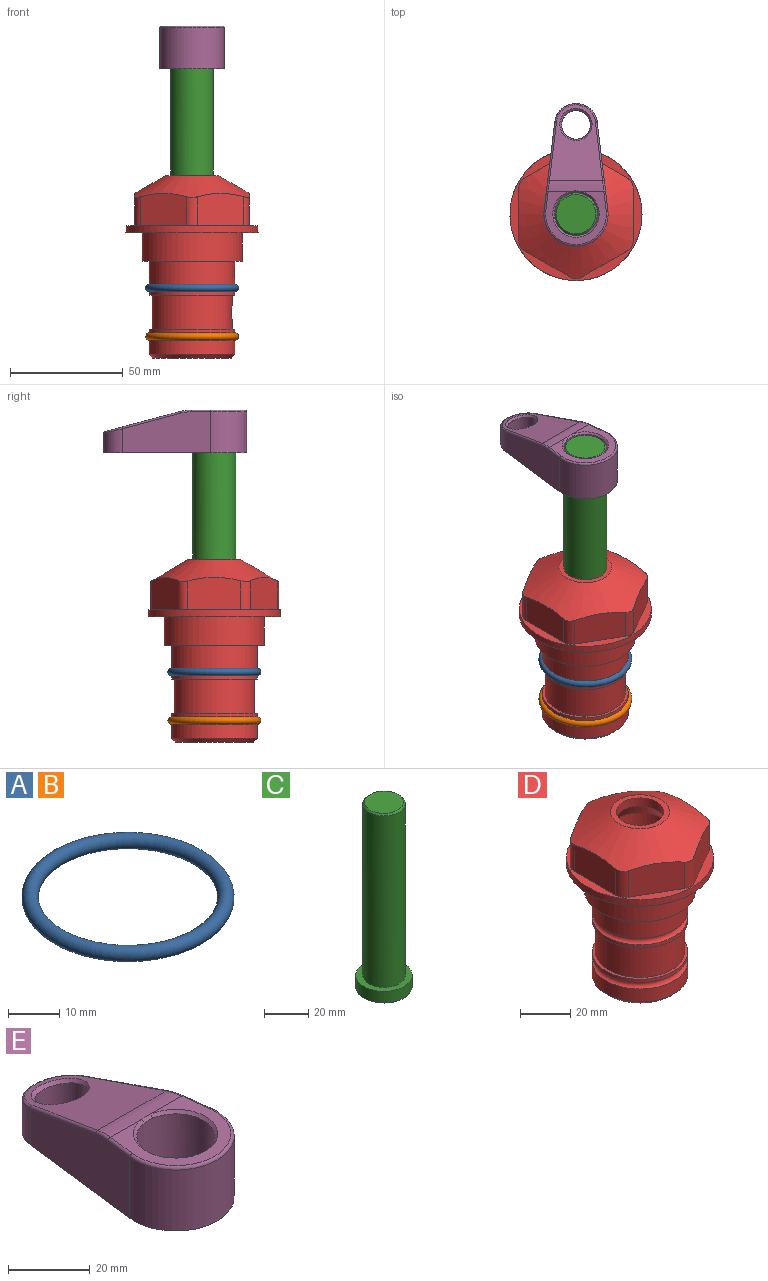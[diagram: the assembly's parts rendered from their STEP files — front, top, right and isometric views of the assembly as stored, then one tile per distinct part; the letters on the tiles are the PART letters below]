
ASSEMBLY  parts=5 mates=4
PART A: 1 faces, bbox 44.7x44.7x3.2 mm
  f0: torus R=19.05mm, axis (0,0,1), area 1193.9mm2
PART B: same geometry as A
PART C: 6 faces, bbox 25.4x25.4x101.6 mm
  f0: plane 17.46x17.46mm, normal (0,0,1), area 239.5mm2, adj f5
  f1: plane 25.4x25.4mm, normal (0,0,-1), area 506.7mm2, adj f2
  f2: cylinder r=12.7mm len=25.4mm, axis (0,0,1), area 506.7mm2, adj f1,f3
  f3: plane 25.4x25.4mm, normal (0,0,1), area 221.7mm2, adj f2,f4
  f4: cylinder r=9.53mm len=94.46mm, axis (0,0,1), area 5653mm2, adj f3,f5
  f5: cone r=8.73mm half-angle=45deg, axis (0,0,-1), area 64.4mm2, adj f0,f4
PART D: 36 faces, bbox 58.7x58.7x81 mm
  f0: cylinder r=17.78mm len=35.56mm, axis (0,0,1), area 1670.8mm2, adj f23,f24,f31
  f1: cylinder r=19.05mm len=38.1mm, axis (0,0,1), area 1191.9mm2, adj f26,f27,f30
  f2: plane 58.66x58.66mm, normal (0,0,-1), area 1150.6mm2, adj f3,f28
  f3: cylinder r=29.33mm len=58.66mm, axis (0,0,-1), area 585.1mm2, adj f2,f4
  f4: plane 58.66x58.66mm, normal (0,0,1), area 475.9mm2, adj f3,f5,f6,f7,f8,f9,f10,f11
  f5: plane 20.32x14.34mm, normal (-0.5,0.87,0), area 324.4mm2, adj f4,f15,f16,f17
  f6: plane 20.32x14.34mm, normal (0.5,0.87,0), area 324.4mm2, adj f4,f14,f15,f17
  f7: plane 23.48x14.34mm, normal (1,0,0), area 324.4mm2, adj f4,f13,f14,f17
  f8: plane 20.32x14.34mm, normal (0.5,-0.87,0), area 324.4mm2, adj f4,f12,f13,f17
  f9: plane 20.32x14.34mm, normal (-0.5,-0.87,0), area 324.4mm2, adj f4,f11,f12,f17
  f10: plane 23.48x14.34mm, normal (-1,0,0), area 324.4mm2, adj f4,f11,f16,f17
  f11: cylinder r=5.08mm len=12.85mm, axis (0,0,-1), area 67.2mm2, adj f4,f9,f10,f17
  f12: cylinder r=5.08mm len=12.85mm, axis (0,0,-1), area 67.2mm2, adj f4,f8,f9,f17
  f13: cylinder r=5.08mm len=12.85mm, axis (0,0,-1), area 67.2mm2, adj f4,f7,f8,f17
  f14: cylinder r=5.08mm len=12.85mm, axis (0,0,-1), area 67.2mm2, adj f4,f6,f7,f17
  f15: cylinder r=5.08mm len=12.85mm, axis (0,0,-1), area 67.2mm2, adj f4,f5,f6,f17
  f16: cylinder r=5.08mm len=12.85mm, axis (0,0,-1), area 67.2mm2, adj f4,f5,f10,f17
  f17: cone r=11.73mm half-angle=60deg, axis (0,0,-1), area 2071.8mm2, adj f5,f6,f7,f8,f9,f10,f11,f12
  f18: plane 23.46x23.46mm, normal (0,0,1), area 147.4mm2, adj f17,f35
  f19: plane 34.93x34.93mm, normal (0,0,-1), area 958mm2, adj f29
  f20: cylinder r=19.05mm len=38.1mm, axis (0,0,1), area 760.1mm2, adj f21,f29
  f21: torus R=19.05mm, axis (0,0,1), area 565.3mm2, adj f20,f22
  f22: cylinder r=19.05mm len=38.1mm, axis (0,0,1), area 190mm2, adj f21,f23
  f23: plane 38.1x38.1mm, normal (0,0,1), area 146.9mm2, adj f0,f22
  f24: plane 38.1x38.1mm, normal (0,0,-1), area 146.9mm2, adj f0,f25
  f25: cylinder r=19.05mm len=38.1mm, axis (0,0,1), area 190mm2, adj f24,f26
  f26: torus R=19.05mm, axis (0,0,1), area 565.3mm2, adj f1,f25
  f27: plane 44.45x44.45mm, normal (0,0,-1), area 411.7mm2, adj f1,f28
  f28: cylinder r=22.23mm len=44.45mm, axis (0,0,1), area 1773.5mm2, adj f2,f27
  f29: cone r=19.05mm half-angle=45deg, axis (0,0,1), area 257.5mm2, adj f19,f20
  f30: cylinder r=3.17mm len=6.75mm, axis (-1,0,0), area 128mm2, adj f1,f33
  f31: cylinder r=3.17mm len=6.35mm, axis (-1,0,0), area 102.5mm2, adj f0,f33
  f32: plane 25.4x25.4mm, normal (0,0,1), area 506.7mm2, adj f33
  f33: cylinder r=12.7mm len=66.42mm, axis (0,0,-1), area 5236.2mm2, adj f30,f31,f32,f34
  f34: cone r=9.53mm half-angle=30deg, axis (0,0,-1), area 443.4mm2, adj f33,f35
  f35: cylinder r=9.53mm len=19.05mm, axis (0,0,-1), area 240.9mm2, adj f18,f34
PART E: 31 faces, bbox 31.7x65.5x19.8 mm
  f0: plane 39.12x18.26mm, normal (0.99,0.12,0), area 612.2mm2, adj f1,f4,f7,f11,f13,f15
  f1: cylinder r=9.53mm len=18.91mm, axis (0,0,-1), area 296.1mm2, adj f0,f2,f7,f17
  f2: plane 39.12x18.26mm, normal (-0.99,0.12,0), area 612.2mm2, adj f1,f4,f7,f12,f14,f16
  f3: cylinder r=6.35mm len=12.7mm, axis (0,0,-1), area 362.4mm2, adj f7,f18
  f4: cylinder r=14.29mm len=28.58mm, axis (0,0,-1), area 882.2mm2, adj f0,f2,f7,f10
  f5: cylinder r=9.53mm len=19.05mm, axis (0,0,-1), area 1092.6mm2, adj f7,f19,f20
  f6: plane 26.99x23.69mm, normal (0,0,1), area 216.2mm2, adj f9,f10,f11,f12,f19
  f7: plane 63.5x28.58mm, normal (0,0,-1), area 661.8mm2, adj f0,f1,f2,f3,f4,f5,f22,f23
  f8: plane 33.52x23.6mm, normal (0,0.26,0.97), area 486mm2, adj f9,f15,f16,f17,f18
  f9: cylinder r=19.05mm len=24.72mm, axis (1,0,0), area 120.4mm2, adj f6,f8,f13,f14,f20
  f10: torus R=13.49mm, axis (0,0,1), area 59mm2, adj f4,f6,f11,f12
  f11: cylinder r=0.79mm len=8.67mm, axis (0.12,-0.99,0), area 10.8mm2, adj f0,f6,f10,f13
  f12: cylinder r=0.79mm len=8.67mm, axis (0.12,0.99,0), area 10.8mm2, adj f2,f6,f10,f14
  f13: bspline ~4.95x1.42mm, area 6.1mm2, adj f0,f9,f11,f15
  f14: bspline ~4.95x1.42mm, area 6.1mm2, adj f2,f9,f12,f16
  f15: cylinder r=0.79mm len=25.95mm, axis (0.12,-0.96,0.26), area 32.9mm2, adj f0,f8,f13,f17
  f16: cylinder r=0.79mm len=25.95mm, axis (0.12,0.96,-0.26), area 32.9mm2, adj f2,f8,f14,f17
  f17: bspline ~18.91x8.38mm, area 30mm2, adj f1,f8,f15,f16
  f18: bspline ~14.29x14.29mm, area 48.3mm2, adj f3,f8
  f19: cone r=9.53mm half-angle=45deg, axis (0,0,1), area 66.5mm2, adj f5,f6,f20
  f20: bspline ~3.22x0.96mm, area 3.5mm2, adj f5,f9,f19
  f21: plane 2.75x2.72mm, normal (0,0,-1), area 2.9mm2, adj f23,f25,f28
  f22: plane 23.05x15.88mm, normal (-0.99,-0.12,0), area 323.6mm2, adj f7,f25,f26,f27,f28,f29
  f23: plane 23.05x15.88mm, normal (0.99,-0.12,0), area 323.6mm2, adj f7,f21,f25,f27,f28,f30
  f24: cylinder r=9.53mm len=10.69mm, axis (0,0,-1), area 114.7mm2, adj f7,f27,f29,f30
  f25: cylinder r=12.7mm len=20.59mm, axis (0,0,-1), area 381.1mm2, adj f7,f21,f22,f23,f26,f28
  f26: plane 2.75x2.72mm, normal (0,0,-1), area 2.9mm2, adj f22,f25,f28
  f27: plane 19.72x18.37mm, normal (0,-0.26,-0.97), area 291.8mm2, adj f22,f23,f24,f28,f29,f30
  f28: cylinder r=15.88mm len=19.92mm, axis (1,0,0), area 54.8mm2, adj f21,f22,f23,f25,f26,f27
  f29: cylinder r=1.59mm len=11mm, axis (0,0,-1), area 34.7mm2, adj f7,f22,f24,f27
  f30: cylinder r=1.59mm len=11mm, axis (0,0,-1), area 34.7mm2, adj f7,f23,f24,f27
PLACE A t=(-23.44,-13.04,11.66)mm
PLACE B t=(-23.44,-13.04,-9.93)mm
PLACE C t=(-23.44,-13.04,39.21)mm
PLACE D t=(-23.44,-13.04,11.66)mm fixed
PLACE E t=(-23.44,-13.04,40.01)mm
MATE fastened E.f4 <-> C.f2  axis (0,0,-1) through (-23.44,-13.04,102.71)mm
MATE fastened B.f0 <-> D.f0  axis (0,0,1) through (-23.44,-13.04,-34.44)mm
MATE cylindrical C.f2 <-> D.f0  axis (0,0,-1) through (-23.44,-13.04,1.11)mm
MATE fastened A.f0 <-> D.f0  axis (0,0,1) through (-23.44,-13.04,-12.85)mm
